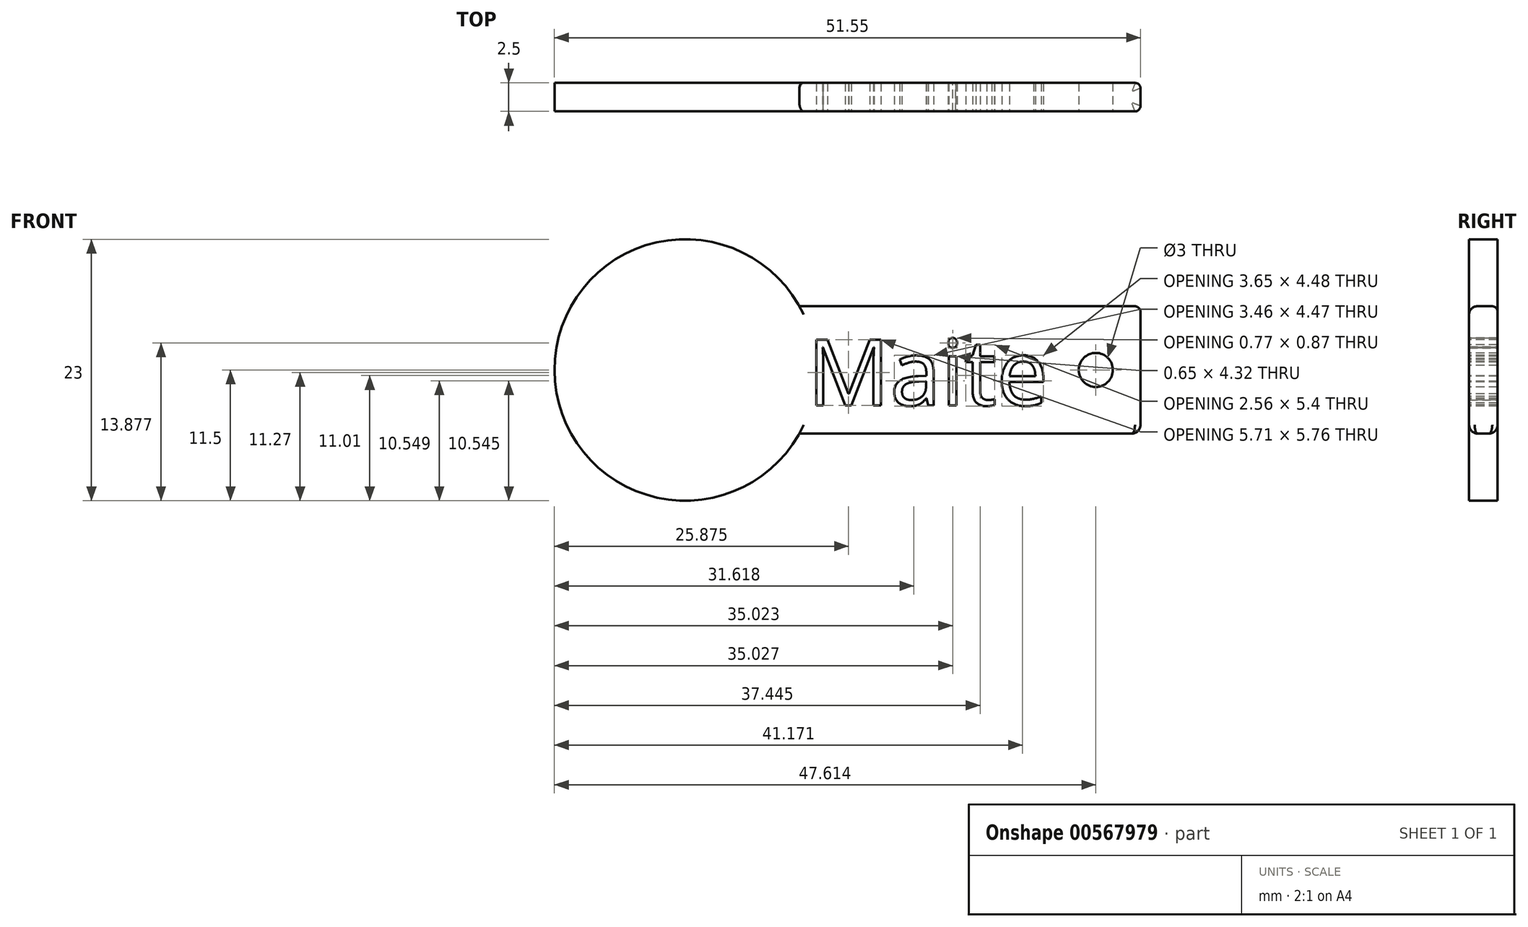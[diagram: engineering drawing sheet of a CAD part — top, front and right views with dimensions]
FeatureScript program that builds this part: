
annotation { "Feature Type Name" : "Feature", "Feature Type Description" : "" }
export const myFeature = defineFeature(function(context is Context, id is Id, definition is map)
    precondition{}
    {
        {
            var Q0;
            Q0=qCreatedBy(makeId("Front.planeOp"),FACE);
            var sketch = newSketch(context, id + "F0", { "sketchPlane" : qUnion([Q0])});
            skCircle(sketch, "E0", {"center": v(-21.17, 0) * mm, "radius": 11.5 * mm});
            skLineSegment(sketch, "E1", {"start": v(-11.12, 5.6) * mm, "end": v(18.88, 5.6) * mm});
            skLineSegment(sketch, "E2", {"start": v(-11.12, -5.6) * mm, "end": v(18.88, -5.6) * mm});
            skLineSegment(sketch, "E3", {"start": v(18.88, 5.6) * mm, "end": v(18.88, -5.6) * mm});
            skSolve(sketch);
        }
        {
            var Q0;
            {var subQ0=sQuery(id+"F0.wireOp",EDGE,"E0");var subQ1=makeQuery(id+"F0.imprint","INTERSECT",VERTEX,{"derivedFrom":[subQ0,sQuery(id+"F0.wireOp",EDGE,"E1")]});Q0=makeQuery(id+"F0.imprint","IMPRINT",FACE,{"disambiguationData":[TD([[makeQuery(id+"F0.imprint","IMPRINT",EDGE,{"disambiguationData":[TD([[subQ1,-1.0]])],"derivedFrom":subQ0}),1.0]])]});}
            var Q1;
            {var subQ0=sQuery(id+"F0.wireOp",EDGE,"E1");Q1=makeQuery(id+"F0.imprint","IMPRINT",FACE,{"disambiguationData":[TD([[makeQuery(id+"F0.imprint","IMPRINT",EDGE,{"derivedFrom":subQ0}),-1.0]])]});}
            extrude(context, id + "F1", {"entities" : qUnion([Q0, Q1]), "depth" : 2.5 * mm, "offsetDistance" : 25 * mm});
        }
        {
            var Q0;
            Q0=makeQuery(id+"F1.opExtrude","CAP_FACE",FACE,{"disambiguationData":[OSD([sQuery(id+"F0.wireOp",EDGE,"E0"),sQuery(id+"F0.wireOp",EDGE,"E1"),sQuery(id+"F0.wireOp",EDGE,"E2"),sQuery(id+"F0.wireOp",EDGE,"E3")])],"isStart":false});
            var sketch = newSketch(context, id + "F2", { "sketchPlane" : qUnion([Q0])});
            skText(sketch, "E4", { "text": "Maite", "fontName": "OpenSans-Regular.ttf"});
            const initialGuessF2  = {"E4": [-0.01044, -0.00311, 1, 0, 0.00581]};
            skSetInitialGuess(sketch, initialGuessF2);
            skSolve(sketch);
        }
        {
            var Q0;
            Q0=makeQuery(id+"F2.imprint","IMPRINT",FACE,{"disambiguationData":[TD([[makeQuery(id+"F2.imprint","IMPRINT",EDGE,{"derivedFrom":sQuery(id+"F2.wireOp",EDGE,"E4.sketch_text.stroke-0")}),-1.0]])]});
            var Q1;
            Q1=makeQuery(id+"F2.imprint","IMPRINT",FACE,{"disambiguationData":[TD([[makeQuery(id+"F2.imprint","IMPRINT",EDGE,{"derivedFrom":sQuery(id+"F2.wireOp",EDGE,"E4.sketch_text.stroke-18")}),-1.0]])]});
            var Q2;
            Q2=makeQuery(id+"F2.imprint","IMPRINT",FACE,{"disambiguationData":[TD([[makeQuery(id+"F2.imprint","IMPRINT",EDGE,{"derivedFrom":sQuery(id+"F2.wireOp",EDGE,"E4.sketch_text.stroke-49")}),-1.0]])]});
            var Q3;
            Q3=makeQuery(id+"F2.imprint","IMPRINT",FACE,{"disambiguationData":[TD([[makeQuery(id+"F2.imprint","IMPRINT",EDGE,{"derivedFrom":sQuery(id+"F2.wireOp",EDGE,"E4.sketch_text.stroke-45")}),-1.0]])]});
            var Q4;
            Q4=makeQuery(id+"F2.imprint","IMPRINT",FACE,{"disambiguationData":[TD([[makeQuery(id+"F2.imprint","IMPRINT",EDGE,{"derivedFrom":sQuery(id+"F2.wireOp",EDGE,"E4.sketch_text.stroke-57")}),-1.0]])]});
            var Q5;
            Q5=makeQuery(id+"F2.imprint","IMPRINT",FACE,{"disambiguationData":[TD([[makeQuery(id+"F2.imprint","IMPRINT",EDGE,{"derivedFrom":sQuery(id+"F2.wireOp",EDGE,"E4.sketch_text.stroke-76")}),-1.0]])]});
            extrude(context, id + "F3", {"entities" : qUnion([Q0, Q1, Q2, Q3, Q4, Q5]), "operationType" : NewBodyOperationType.REMOVE, "oppositeDirection" : true, "depth" : 25 * mm, "offsetDistance" : 25 * mm});
        }
        {
            var Q0;
            {var subQ0=sQuery(id+"F0.wireOp",EDGE,"E2");var subQ1=sQuery(id+"F0.wireOp",EDGE,"E0");var subQ2=sQuery(id+"F0.wireOp",EDGE,"E3");var subQ3=sQuery(id+"F0.wireOp",EDGE,"E1");Q0=makeQuery(id+"F3.boolean.opBoolean","SPLIT",FACE,{"disambiguationData":[TD([makeQuery(id+"F1.opExtrude","SWEPT_FACE",FACE,{"disambiguationData":[OSD([subQ1])]})])],"derivedFrom":makeQuery(id+"F1.opExtrude","CAP_FACE",FACE,{"disambiguationData":[OSD([subQ1,subQ3,subQ0,subQ2])],"isStart":false})});}
            var sketch = newSketch(context, id + "F4", { "sketchPlane" : qUnion([Q0])});
            skCircle(sketch, "E5", {"center": v(14.94, 0) * mm, "radius": 1.5 * mm});
            skSolve(sketch);
        }
        {
            var Q0;
            Q0=makeQuery(id+"F4.imprint","IMPRINT",FACE,{"disambiguationData":[TD([[makeQuery(id+"F4.imprint","IMPRINT",EDGE,{"derivedFrom":sQuery(id+"F4.wireOp",EDGE,"E5")}),1.0]])]});
            extrude(context, id + "F5", {"entities" : qUnion([Q0]), "operationType" : NewBodyOperationType.REMOVE, "oppositeDirection" : true, "depth" : 25 * mm, "offsetDistance" : 25 * mm});
        }
        {
            var Q0;
            Q0=makeQuery(id+"F1.opExtrude","CAP_EDGE",EDGE,{"disambiguationData":[OSD([sQuery(id+"F0.wireOp",EDGE,"E1")])],"isStart":false});
            fillet(context, id + "F6", {"entities" : qUnion([Q0]), "radius" : 0.72 * mm, "tangentPropagation" : true, "allowEdgeOverflow" : false});
        }
        {
            var Q0;
            Q0=makeQuery(id+"F1.opExtrude","CAP_EDGE",EDGE,{"disambiguationData":[OSD([sQuery(id+"F0.wireOp",EDGE,"E3")])],"isStart":false});
            fillet(context, id + "F7", {"entities" : qUnion([Q0]), "radius" : 0.48 * mm, "tangentPropagation" : true, "allowEdgeOverflow" : false});
        }
        {
            var Q0;
            Q0=makeQuery(id+"F1.opExtrude","CAP_EDGE",EDGE,{"disambiguationData":[OSD([sQuery(id+"F0.wireOp",EDGE,"E3")])],"isStart":true});
            fillet(context, id + "F8", {"entities" : qUnion([Q0]), "radius" : 0.46 * mm, "tangentPropagation" : true, "allowEdgeOverflow" : false});
        }
        {
            var Q0;
            Q0=makeQuery(id+"F1.opExtrude","CAP_EDGE",EDGE,{"disambiguationData":[OSD([sQuery(id+"F0.wireOp",EDGE,"E2")])],"isStart":false});
            fillet(context, id + "F9", {"entities" : qUnion([Q0]), "radius" : 0.77 * mm, "tangentPropagation" : true, "allowEdgeOverflow" : false});
        }
    });
